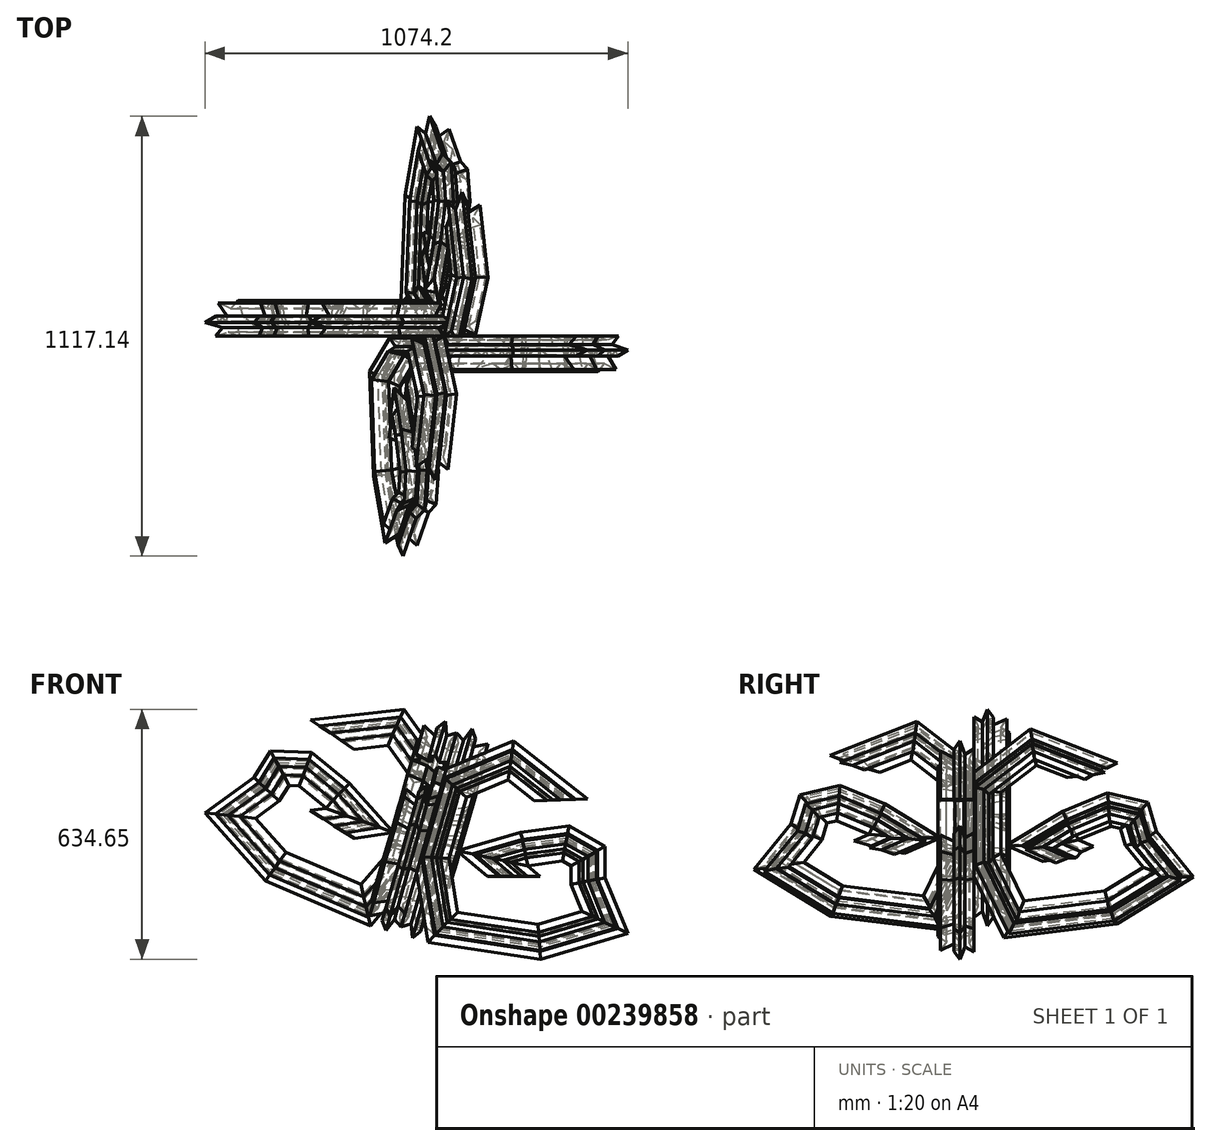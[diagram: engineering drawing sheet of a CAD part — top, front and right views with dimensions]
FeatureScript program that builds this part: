
annotation { "Feature Type Name" : "Feature", "Feature Type Description" : "" }
export const myFeature = defineFeature(function(context is Context, id is Id, definition is map)
    precondition{}
    {
        {
            var Q0;
            Q0=qCreatedBy(makeId("Top.planeOp"),FACE);
            var sketch = newSketch(context, id + "F0", { "sketchPlane" : qUnion([Q0])});
            skLineSegment(sketch, "E0", {"start": v(-15.85, -5.64) * mm, "end": v(-40.54, -40.7) * mm});
            skLineSegment(sketch, "E1", {"start": v(-40.54, -40.7) * mm, "end": v(-7.32, -25.76) * mm});
            skLineSegment(sketch, "E2", {"start": v(-7.32, -25.76) * mm, "end": v(12.2, -46.79) * mm});
            skLineSegment(sketch, "E3", {"start": v(12.2, -46.79) * mm, "end": v(27.43, -4.42) * mm});
            skLineSegment(sketch, "E4", {"start": v(27.43, -4.42) * mm, "end": v(58.83, 19.05) * mm});
            skLineSegment(sketch, "E5", {"start": v(58.83, 19.05) * mm, "end": v(12.2, 21.8) * mm});
            skLineSegment(sketch, "E6", {"start": v(12.2, 21.8) * mm, "end": v(17.98, 43.74) * mm});
            skLineSegment(sketch, "E7", {"start": v(17.98, 43.74) * mm, "end": v(-14.02, 33.38) * mm});
            skLineSegment(sketch, "E8", {"start": v(-14.02, 33.38) * mm, "end": v(-47.55, 43.74) * mm});
            skLineSegment(sketch, "E9", {"start": v(-47.55, 43.74) * mm, "end": v(-28.35, 21.8) * mm});
            skLineSegment(sketch, "E10", {"start": v(-28.35, 21.8) * mm, "end": v(-74.98, 8.69) * mm});
            skLineSegment(sketch, "E11", {"start": v(-74.98, 8.69) * mm, "end": v(-45.42, -6.86) * mm});
            skLineSegment(sketch, "E12", {"start": v(-45.42, -6.86) * mm, "end": v(-38.56, 6.18) * mm});
            skLineSegment(sketch, "E13", {"start": v(-38.56, 6.18) * mm, "end": v(-28.65, -5.33) * mm});
            skLineSegment(sketch, "E14", {"start": v(-28.65, -5.33) * mm, "end": v(-20.4, 6.38) * mm});
            skLineSegment(sketch, "E15", {"start": v(-20.4, 6.38) * mm, "end": v(-15.85, -5.64) * mm});
            skSolve(sketch);
        }
        {
            var Q0;
            Q0=qCreatedBy(makeId("Front.planeOp"),FACE);
            var sketch = newSketch(context, id + "F1", { "sketchPlane" : qUnion([Q0])});
            skLineSegment(sketch, "E16", {"start": v(0, 0) * mm, "end": v(-51.51, 43.74) * mm});
            skLineSegment(sketch, "E17", {"start": v(-51.51, 43.74) * mm, "end": v(19.81, 64.47) * mm});
            skLineSegment(sketch, "E18", {"start": v(19.81, 64.47) * mm, "end": v(123.14, 78.18) * mm});
            skLineSegment(sketch, "E19", {"start": v(123.14, 78.18) * mm, "end": v(175.56, 48.31) * mm});
            skLineSegment(sketch, "E20", {"start": v(175.56, 48.31) * mm, "end": v(175.56, -12.95) * mm});
            skLineSegment(sketch, "E21", {"start": v(175.56, -12.95) * mm, "end": v(216.81, -113.72) * mm});
            skLineSegment(sketch, "E22", {"start": v(216.81, -113.72) * mm, "end": v(56.83, -160.96) * mm});
            skLineSegment(sketch, "E23", {"start": v(56.83, -160.96) * mm, "end": v(-183.68, -124.45) * mm});
            skLineSegment(sketch, "E24", {"start": v(-183.68, -124.45) * mm, "end": v(-211.6, 48.31) * mm});
            skLineSegment(sketch, "E25", {"start": v(-211.6, 48.31) * mm, "end": v(-160.06, 228.8) * mm});
            skLineSegment(sketch, "E26", {"start": v(-160.06, 228.8) * mm, "end": v(-16.18, 288.92) * mm});
            skLineSegment(sketch, "E27", {"start": v(-16.18, 288.92) * mm, "end": v(104.07, 194.44) * mm});
            skSolve(sketch);
        }
        {
            var Q0;
            Q0=makeQuery(id+"F0.imprint","IMPRINT",FACE,{"disambiguationData":[TD([[makeQuery(id+"F0.imprint","IMPRINT",EDGE,{"derivedFrom":sQuery(id+"F0.wireOp",EDGE,"E0")}),1.0]])]});
            var Q1;
            Q1=sQuery(id+"F1.wireOp",EDGE,"E16");
            var Q2;
            Q2=sQuery(id+"F1.wireOp",EDGE,"E17");
            var Q3;
            Q3=sQuery(id+"F1.wireOp",EDGE,"E18");
            var Q4;
            Q4=sQuery(id+"F1.wireOp",EDGE,"E19");
            var Q5;
            Q5=sQuery(id+"F1.wireOp",EDGE,"E20");
            var Q6;
            Q6=sQuery(id+"F1.wireOp",EDGE,"E21");
            var Q7;
            Q7=sQuery(id+"F1.wireOp",EDGE,"E22");
            var Q8;
            Q8=sQuery(id+"F1.wireOp",EDGE,"E23");
            var Q9;
            Q9=sQuery(id+"F1.wireOp",EDGE,"E24");
            var Q10;
            Q10=sQuery(id+"F1.wireOp",EDGE,"E25");
            var Q11;
            Q11=sQuery(id+"F1.wireOp",EDGE,"E26");
            var Q12;
            Q12=sQuery(id+"F1.wireOp",EDGE,"E27");
            sweep(context, id + "F2", {"profiles" : qUnion([Q0]), "path" : qUnion([Q1, Q2, Q3, Q4, Q5, Q6, Q7, Q8, Q9, Q10, Q11, Q12])});
        }
        {
            var Q0;
            Q0=makeQuery(id+"F2.opSweep","SWEPT_BODY",BODY,{"disambiguationData":[OSD([sQuery(id+"F0.wireOp",EDGE,"E0"),sQuery(id+"F0.wireOp",EDGE,"E1"),sQuery(id+"F0.wireOp",EDGE,"E2"),sQuery(id+"F0.wireOp",EDGE,"E3"),sQuery(id+"F0.wireOp",EDGE,"E4"),sQuery(id+"F0.wireOp",EDGE,"E5"),sQuery(id+"F0.wireOp",EDGE,"E6"),sQuery(id+"F0.wireOp",EDGE,"E7"),sQuery(id+"F0.wireOp",EDGE,"E8"),sQuery(id+"F0.wireOp",EDGE,"E9"),sQuery(id+"F0.wireOp",EDGE,"E10"),sQuery(id+"F0.wireOp",EDGE,"E11"),sQuery(id+"F0.wireOp",EDGE,"E12"),sQuery(id+"F0.wireOp",EDGE,"E13"),sQuery(id+"F0.wireOp",EDGE,"E14"),sQuery(id+"F0.wireOp",EDGE,"E15"),sQuery(id+"F1.wireOp",EDGE,"E27")])]});
            var Q1;
            Q1=makeQuery(id+"F2.opSweep","SWEPT_EDGE",EDGE,{"disambiguationData":[OSD([sQuery(id+"F0.wireOp",EDGE,"E8"),sQuery(id+"F0.wireOp",EDGE,"E9"),sQuery(id+"F1.wireOp",EDGE,"E25")])]});
            circularPattern(context, id + "F3", {"entities" : qUnion([Q0]), "axis" : qUnion([Q1]), "angle" : 360 * degree, "instanceCount" : 4, "equalSpace" : true});
        }
        {
            var Q0;
            Q0=makeQuery(id+"F2.opSweep","SWEPT_BODY",BODY,{"disambiguationData":[OSD([sQuery(id+"F0.wireOp",EDGE,"E0"),sQuery(id+"F0.wireOp",EDGE,"E1"),sQuery(id+"F0.wireOp",EDGE,"E2"),sQuery(id+"F0.wireOp",EDGE,"E3"),sQuery(id+"F0.wireOp",EDGE,"E4"),sQuery(id+"F0.wireOp",EDGE,"E5"),sQuery(id+"F0.wireOp",EDGE,"E6"),sQuery(id+"F0.wireOp",EDGE,"E7"),sQuery(id+"F0.wireOp",EDGE,"E8"),sQuery(id+"F0.wireOp",EDGE,"E9"),sQuery(id+"F0.wireOp",EDGE,"E10"),sQuery(id+"F0.wireOp",EDGE,"E11"),sQuery(id+"F0.wireOp",EDGE,"E12"),sQuery(id+"F0.wireOp",EDGE,"E13"),sQuery(id+"F0.wireOp",EDGE,"E14"),sQuery(id+"F0.wireOp",EDGE,"E15"),sQuery(id+"F1.wireOp",EDGE,"E27")])]});
            var Q1;
            Q1=makeQuery(id+"F3.opPattern","COPY",BODY,{"derivedFrom":makeQuery(id+"F2.opSweep","SWEPT_BODY",BODY,{"disambiguationData":[OSD([sQuery(id+"F0.wireOp",EDGE,"E0"),sQuery(id+"F0.wireOp",EDGE,"E1"),sQuery(id+"F0.wireOp",EDGE,"E2"),sQuery(id+"F0.wireOp",EDGE,"E3"),sQuery(id+"F0.wireOp",EDGE,"E4"),sQuery(id+"F0.wireOp",EDGE,"E5"),sQuery(id+"F0.wireOp",EDGE,"E6"),sQuery(id+"F0.wireOp",EDGE,"E7"),sQuery(id+"F0.wireOp",EDGE,"E8"),sQuery(id+"F0.wireOp",EDGE,"E9"),sQuery(id+"F0.wireOp",EDGE,"E10"),sQuery(id+"F0.wireOp",EDGE,"E11"),sQuery(id+"F0.wireOp",EDGE,"E12"),sQuery(id+"F0.wireOp",EDGE,"E13"),sQuery(id+"F0.wireOp",EDGE,"E14"),sQuery(id+"F0.wireOp",EDGE,"E15"),sQuery(id+"F1.wireOp",EDGE,"E27")])]}),"instanceName":"1"});
            var Q2;
            Q2=makeQuery(id+"F3.opPattern","COPY",BODY,{"derivedFrom":makeQuery(id+"F2.opSweep","SWEPT_BODY",BODY,{"disambiguationData":[OSD([sQuery(id+"F0.wireOp",EDGE,"E0"),sQuery(id+"F0.wireOp",EDGE,"E1"),sQuery(id+"F0.wireOp",EDGE,"E2"),sQuery(id+"F0.wireOp",EDGE,"E3"),sQuery(id+"F0.wireOp",EDGE,"E4"),sQuery(id+"F0.wireOp",EDGE,"E5"),sQuery(id+"F0.wireOp",EDGE,"E6"),sQuery(id+"F0.wireOp",EDGE,"E7"),sQuery(id+"F0.wireOp",EDGE,"E8"),sQuery(id+"F0.wireOp",EDGE,"E9"),sQuery(id+"F0.wireOp",EDGE,"E10"),sQuery(id+"F0.wireOp",EDGE,"E11"),sQuery(id+"F0.wireOp",EDGE,"E12"),sQuery(id+"F0.wireOp",EDGE,"E13"),sQuery(id+"F0.wireOp",EDGE,"E14"),sQuery(id+"F0.wireOp",EDGE,"E15"),sQuery(id+"F1.wireOp",EDGE,"E27")])]}),"instanceName":"2"});
            var Q3;
            Q3=makeQuery(id+"F3.opPattern","COPY",BODY,{"derivedFrom":makeQuery(id+"F2.opSweep","SWEPT_BODY",BODY,{"disambiguationData":[OSD([sQuery(id+"F0.wireOp",EDGE,"E0"),sQuery(id+"F0.wireOp",EDGE,"E1"),sQuery(id+"F0.wireOp",EDGE,"E2"),sQuery(id+"F0.wireOp",EDGE,"E3"),sQuery(id+"F0.wireOp",EDGE,"E4"),sQuery(id+"F0.wireOp",EDGE,"E5"),sQuery(id+"F0.wireOp",EDGE,"E6"),sQuery(id+"F0.wireOp",EDGE,"E7"),sQuery(id+"F0.wireOp",EDGE,"E8"),sQuery(id+"F0.wireOp",EDGE,"E9"),sQuery(id+"F0.wireOp",EDGE,"E10"),sQuery(id+"F0.wireOp",EDGE,"E11"),sQuery(id+"F0.wireOp",EDGE,"E12"),sQuery(id+"F0.wireOp",EDGE,"E13"),sQuery(id+"F0.wireOp",EDGE,"E14"),sQuery(id+"F0.wireOp",EDGE,"E15"),sQuery(id+"F1.wireOp",EDGE,"E27")])]}),"instanceName":"3"});
            var Q4;
            Q4=qCreatedBy(makeId("Origin.pointOp"),VERTEX);
            var Q5;
            Q5=makeQuery(id+"F2.opSweep","SWEPT_EDGE",EDGE,{"disambiguationData":[OSD([sQuery(id+"F0.wireOp",EDGE,"E0"),sQuery(id+"F0.wireOp",EDGE,"E1"),sQuery(id+"F1.wireOp",EDGE,"E19")])]});
            transform(context, id + "F4", {"entities" : qUnion([Q0, Q1, Q2, Q3]), "transformType" : TransformType.TRANSLATION_ENTITY, "oppositeDirectionEntity" : false, "transformLine" : qUnion([Q4, Q5]), "makeCopy" : false});
        }
    });
